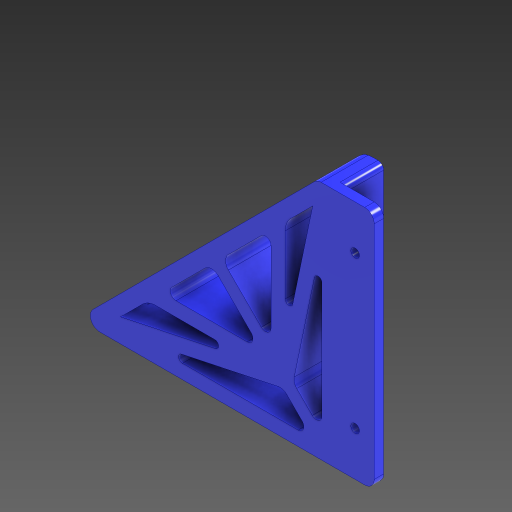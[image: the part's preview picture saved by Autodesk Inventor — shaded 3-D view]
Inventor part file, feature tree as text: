
AUTODESK INVENTOR PART (.ipt)
format: ipt  version: 2024 (Build 280153000, 153)  size: 582,656 bytes
history: native  units: mm
features: fillet x7, sketch x6, extrude x5, projected_geometry x3, hole x2, chamfer x1
ambient origin geometry x8: Origin, YZ Plane, XZ Plane, XY Plane, X Axis, Y Axis, Z Axis, Center Point
bodies: Body1 (feature_tree)
feature tree (24):
  extrude  "Extrusion3"  Depth=4.0mm
  fillet  "Fillet2"  Radius=175.0mm
  hole  "Hole4"  [1 undecoded]
  sketch  "Sketch7"  dims[d46=5.0mm]
  extrude  "Extrusion5"  Depth=10.0mm
  extrude  "Extrusion6"  Depth=23.285mm
  fillet  "Fillet4"  Radius=7.5mm
  fillet  "Fillet6"  Radius=20.0mm
  extrude  "Extrusion7"  Depth=10.0mm
  hole  "Hole6"  [1 undecoded]
  fillet  "Fillet9"  Radius=7.5mm
  fillet  "Fillet10"  Radius=20.0mm
  fillet  "Fillet11"  Radius=7.5mm
  extrude  "Extrusion9"  TaperAngle=0.0deg  [1 undecoded]
  chamfer  "Chamfer1"  Distance=3.0mm
  fillet  "Fillet13"  Radius=3.75mm
  sketch  "Sketch1"  dims[d3=30.0mm d41=4.0mm d42=175.0mm]
  sketch  "Sketch6"  dims[d43=45.0deg d44=5.0mm d45=0.0mm]
  sketch  "Sketch10"  dims[d47=4.5mm d48=6.0mm d49=9.4mm d50=2.0mm d51=90.0deg d52=39.95mm d53=0.0mm d54=10.0mm]
  sketch  "Sketch11"  dims[d55=80.0mm d56=23.285mm d57=7.5mm d58=20.0mm]
  sketch  "Sketch13"  dims[d61=7.5mm d63=7.5mm d66=3.75mm d67=7.5mm d68=20.0mm d69=0.0mm d70=7.5mm d71=0.0mm d72=0.0mm d74=3.0mm d75=3.75mm d77=5.0mm d91=10.0mm d93=15.0mm d95=62.25mm d96=15.24mm d97=10.0mm d98=0.0mm d101=6.2mm d102=6.0mm d103=9.4mm d104=2.0mm d105=90.0deg d106=8.0mm d107=0.0mm d108=7.62mm d111=54.952633mm d112=49.952633mm d115=3.0mm d116=8.0mm d117=2.0mm d119=10.0mm d120=0.0mm d121=2.0mm d122=2.0mm d123=45.0deg d124=10.0mm d118=0.0mm d125=0.5mm d126=0.872665mm d127=0.5mm d128=0.872665mm]
  projected_geometry  "Projected Loop3"
  projected_geometry  "Projected Loop4"
  projected_geometry  "Project Cut Edges1"
note: 3 required parameter values undecoded (feature->parameter linkage not recoverable at this tier; creation-order binding heuristic only, values carry confidence <= 0.55)
